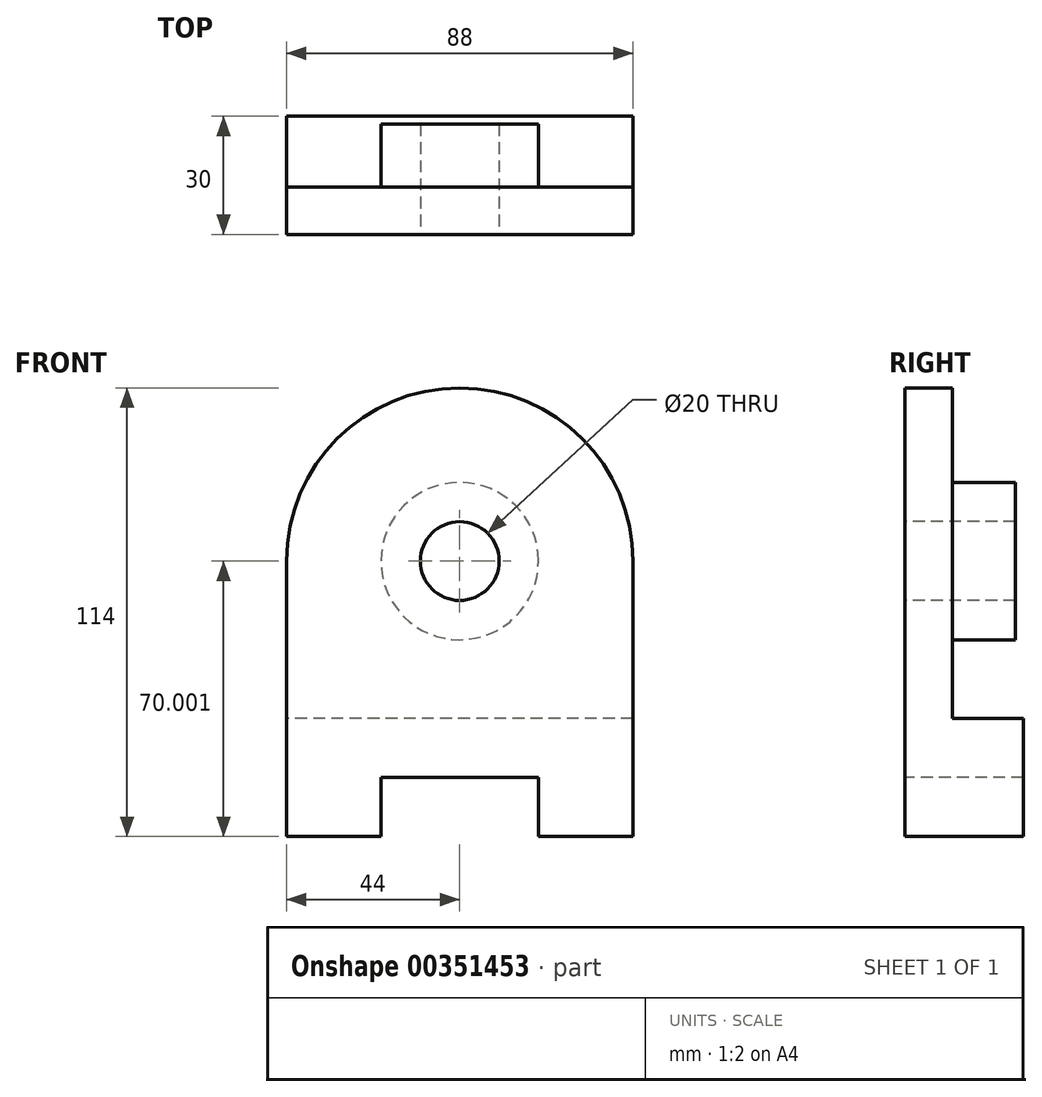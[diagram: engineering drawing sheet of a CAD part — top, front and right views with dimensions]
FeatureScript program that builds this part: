
annotation { "Feature Type Name" : "Feature", "Feature Type Description" : "" }
export const myFeature = defineFeature(function(context is Context, id is Id, definition is map)
    precondition{}
    {
        {
            var Q0;
            Q0=qCreatedBy(makeId("Front.planeOp"),FACE);
            var sketch = newSketch(context, id + "F0", { "sketchPlane" : qUnion([Q0])});
            skLineSegment(sketch, "E0", {"start": v(-44, -29.37) * mm, "end": v(-20, -29.37) * mm});
            skLineSegment(sketch, "E1", {"start": v(44, -29.37) * mm, "end": v(20, -29.37) * mm});
            skLineSegment(sketch, "E2", {"start": v(20, -29.37) * mm, "end": v(20, -14.37) * mm});
            skLineSegment(sketch, "E3", {"start": v(20, -14.37) * mm, "end": v(-20, -14.37) * mm});
            skLineSegment(sketch, "E4", {"start": v(-20, -14.37) * mm, "end": v(-20, -29.37) * mm});
            skLineSegment(sketch, "E5", {"start": v(-44, -29.37) * mm, "end": v(-44, 0.63) * mm});
            skLineSegment(sketch, "E6", {"start": v(-44, 0.63) * mm, "end": v(44, 0.63) * mm});
            skLineSegment(sketch, "E7", {"start": v(44, 0.63) * mm, "end": v(44, -29.37) * mm});
            skLineSegment(sketch, "E8", {"start": v(-44, -29.37) * mm, "end": v(-44, 0.63) * mm, "construction": true});
            skLineSegment(sketch, "E9", {"start": v(-44, 40.63) * mm, "end": v(0, 40.63) * mm, "construction": true});
            skCircle(sketch, "E10", {"center": v(0, 40.63) * mm, "radius": 20 * mm});
            skCircle(sketch, "E11", {"center": v(0, 40.63) * mm, "radius": 10 * mm});
            skArc(sketch, "E12", {"start": v(44, 40.63) * mm, "mid": v(0, 84.63) * mm, "end": v(-44, 40.63) * mm});
            skLineSegment(sketch, "E13", {"start": v(44, 0.63) * mm, "end": v(44, 40.63) * mm});
            skLineSegment(sketch, "E14", {"start": v(-44, 40.63) * mm, "end": v(-44, 0.63) * mm});
            skSolve(sketch);
        }
        {
            var Q0;
            Q0=makeQuery(id+"F0.imprint","IMPRINT",FACE,{"disambiguationData":[TD([[makeQuery(id+"F0.imprint","IMPRINT",EDGE,{"derivedFrom":sQuery(id+"F0.wireOp",EDGE,"E0")}),1.0]])]});
            extrude(context, id + "F1", {"entities" : qUnion([Q0]), "oppositeDirection" : true, "depth" : 30 * mm});
        }
        {
            var Q0;
            Q0 = qSketchRegion(id + "F0", true);
            extrude(context, id + "F2", {"entities" : qUnion([Q0]), "operationType" : NewBodyOperationType.ADD, "oppositeDirection" : true, "depth" : 12 * mm});
        }
        {
            var Q0;
            Q0=makeQuery(id+"F0.imprint","IMPRINT",FACE,{"disambiguationData":[TD([[makeQuery(id+"F0.imprint","IMPRINT",EDGE,{"derivedFrom":sQuery(id+"F0.wireOp",EDGE,"E10")}),1.0]])]});
            extrude(context, id + "F3", {"entities" : qUnion([Q0]), "operationType" : NewBodyOperationType.ADD, "oppositeDirection" : true, "depth" : 28 * mm});
        }
    });
